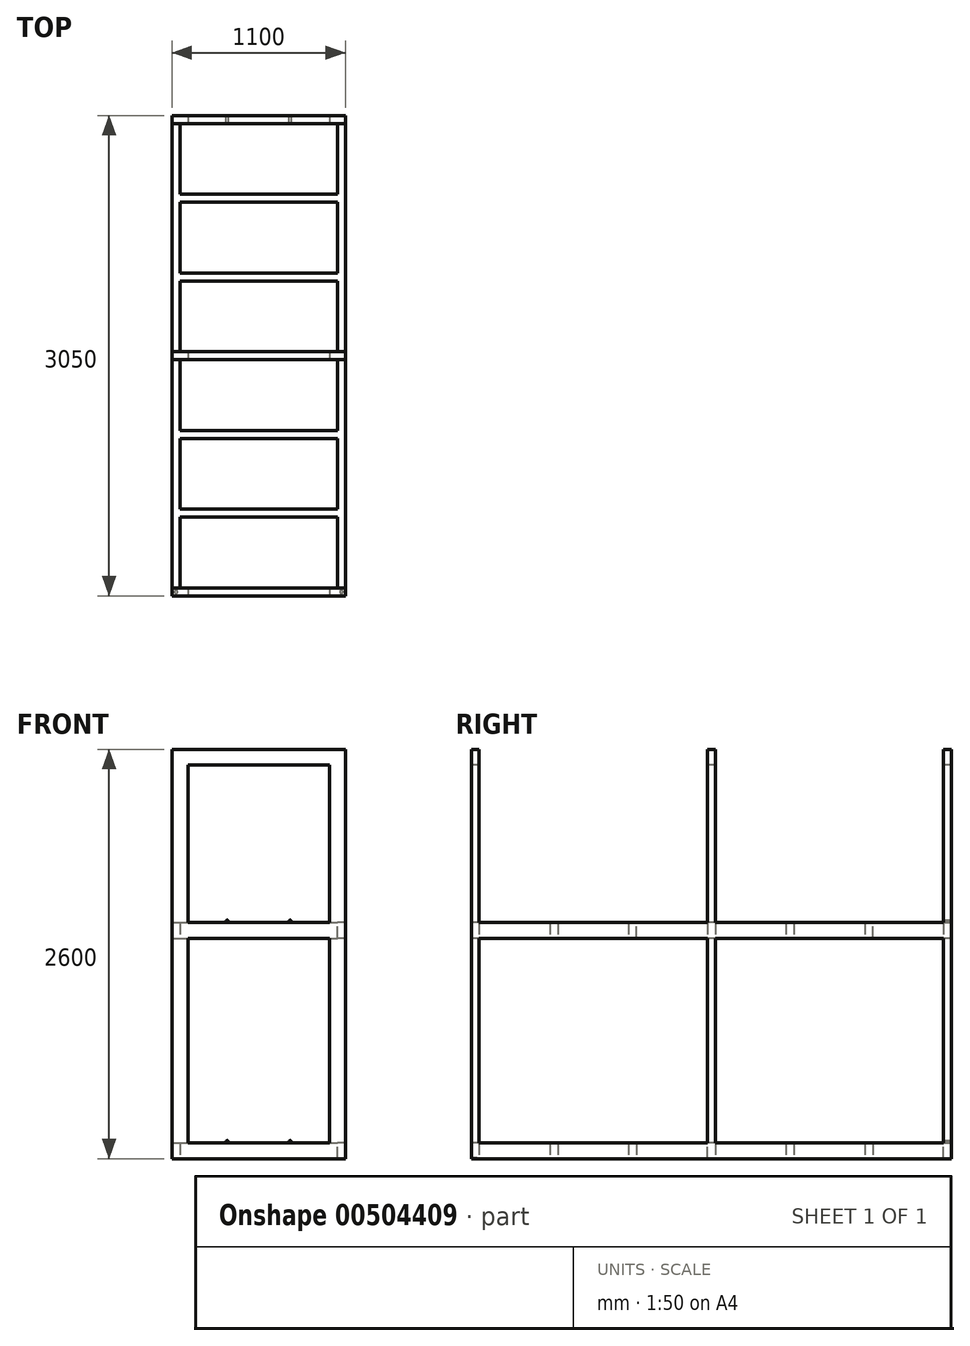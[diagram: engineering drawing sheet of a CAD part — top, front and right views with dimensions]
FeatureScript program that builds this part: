
annotation { "Feature Type Name" : "Feature", "Feature Type Description" : "" }
export const myFeature = defineFeature(function(context is Context, id is Id, definition is map)
    precondition{}
    {
        {
            var Q0;
            Q0=qCreatedBy(makeId("Front.planeOp"),FACE);
            var sketch = newSketch(context, id + "F0", { "sketchPlane" : qUnion([Q0])});
            skCircle(sketch, "E0", {"center": v(0, 700) * mm, "radius": 600 * mm});
            skCircle(sketch, "E1", {"center": v(0, 2100) * mm, "radius": 600 * mm});
            skSolve(sketch);
        }
        {
            var Q0;
            Q0=qCreatedBy(makeId("Front.planeOp"),FACE);
            var sketch = newSketch(context, id + "F1", { "sketchPlane" : qUnion([Q0])});
            skLineSegment(sketch, "E2.bottom", {"start": v(-550, 2600) * mm, "end": v(550, 2600) * mm});
            skLineSegment(sketch, "E2.top", {"start": v(-550, 0) * mm, "end": v(550, 0) * mm});
            skLineSegment(sketch, "E2.left", {"start": v(-550, 2600) * mm, "end": v(-550, 0) * mm});
            skLineSegment(sketch, "E2.right", {"start": v(550, 2600) * mm, "end": v(550, 0) * mm});
            skSolve(sketch);
        }
        {
            var Q0;
            Q0=makeQuery(id+"F1.imprint","IMPRINT",FACE,{"disambiguationData":[TD([[makeQuery(id+"F1.imprint","IMPRINT",EDGE,{"derivedFrom":sQuery(id+"F1.wireOp",EDGE,"E2.bottom")}),-1.0]])]});
            extrude(context, id + "F2", {"entities" : qUnion([Q0]), "depth" : 4550 * mm, "offsetDistance" : 25 * mm});
        }
        {
            var Q0;
            Q0=makeQuery(id+"F2.opExtrude","CAP_FACE",FACE,{"disambiguationData":[OSD([sQuery(id+"F1.wireOp",EDGE,"E2.bottom"),sQuery(id+"F1.wireOp",EDGE,"E2.top"),sQuery(id+"F1.wireOp",EDGE,"E2.left"),sQuery(id+"F1.wireOp",EDGE,"E2.right")])],"isStart":false});
            var sketch = newSketch(context, id + "F3", { "sketchPlane" : qUnion([Q0])});
            skLineSegment(sketch, "E3.bottom", {"start": v(-450, 1400) * mm, "end": v(450, 1400) * mm});
            skLineSegment(sketch, "E3.top", {"start": v(-450, 100) * mm, "end": v(450, 100) * mm});
            skLineSegment(sketch, "E3.left", {"start": v(-450, 1400) * mm, "end": v(-450, 100) * mm});
            skLineSegment(sketch, "E3.right", {"start": v(450, 1400) * mm, "end": v(450, 100) * mm});
            skLineSegment(sketch, "E4.top", {"start": v(-450, 1500) * mm, "end": v(450, 1500) * mm});
            skLineSegment(sketch, "E5.bottom", {"start": v(-450, 2500) * mm, "end": v(450, 2500) * mm});
            skLineSegment(sketch, "E6", {"start": v(-450, 1500) * mm, "end": v(-450, 2500) * mm});
            skLineSegment(sketch, "E7", {"start": v(450, 2500) * mm, "end": v(450, 1500) * mm});
            skSolve(sketch);
        }
        {
            var Q0;
            Q0=qSketchRegion(id+"F3",true);
            extrude(context, id + "F4", {"entities" : qUnion([Q0]), "operationType" : NewBodyOperationType.REMOVE, "oppositeDirection" : true, "depth" : 20000 * mm, "offsetDistance" : 25 * mm});
        }
        {
            var Q0;
            Q0=makeQuery(id+"F2.opExtrude","SWEPT_FACE",FACE,{"disambiguationData":[OSD([sQuery(id+"F1.wireOp",EDGE,"E2.right")])]});
            var sketch = newSketch(context, id + "F5", { "sketchPlane" : qUnion([Q0])});
            skLineSegment(sketch, "E8.bottom", {"start": v(-1550, 4014.4) * mm, "end": v(-3000, 4014.4) * mm});
            skLineSegment(sketch, "E8.top", {"start": v(-1550, -275.7) * mm, "end": v(-3000, -275.7) * mm});
            skLineSegment(sketch, "E8.left", {"start": v(-1550, 4014.4) * mm, "end": v(-1550, -275.7) * mm});
            skLineSegment(sketch, "E8.right", {"start": v(-3000, 4014.4) * mm, "end": v(-3000, -275.7) * mm});
            skLineSegment(sketch, "E9.bottom", {"start": v(-3050, 4012.1) * mm, "end": v(-4500, 4012.1) * mm});
            skLineSegment(sketch, "E9.top", {"start": v(-3050, -275.7) * mm, "end": v(-4500, -275.7) * mm});
            skLineSegment(sketch, "E9.left", {"start": v(-3050, 4012.1) * mm, "end": v(-3050, -275.7) * mm});
            skLineSegment(sketch, "E9.right", {"start": v(-4500, 4012.1) * mm, "end": v(-4500, -275.7) * mm});
            skSolve(sketch);
        }
        {
            var Q0;
            Q0=qSketchRegion(id+"F5",true);
            extrude(context, id + "F6", {"entities" : qUnion([Q0]), "operationType" : NewBodyOperationType.REMOVE, "oppositeDirection" : true, "depth" : 2000 * mm, "offsetDistance" : 25 * mm});
        }
        {
            var Q0;
            Q0=makeQuery(id+"F2.opExtrude","CAP_FACE",FACE,{"disambiguationData":[OSD([sQuery(id+"F1.wireOp",EDGE,"E2.bottom"),sQuery(id+"F1.wireOp",EDGE,"E2.top"),sQuery(id+"F1.wireOp",EDGE,"E2.left"),sQuery(id+"F1.wireOp",EDGE,"E2.right")])],"isStart":false});
            var sketch = newSketch(context, id + "F7", { "sketchPlane" : qUnion([Q0])});
            skLineSegment(sketch, "E10.bottom", {"start": v(550, 1500) * mm, "end": v(500, 1500) * mm});
            skLineSegment(sketch, "E10.top", {"start": v(550, 1400) * mm, "end": v(500, 1400) * mm});
            skLineSegment(sketch, "E10.left", {"start": v(550, 1500) * mm, "end": v(550, 1400) * mm});
            skLineSegment(sketch, "E10.right", {"start": v(500, 1500) * mm, "end": v(500, 1400) * mm});
            skLineSegment(sketch, "E11.left", {"start": v(550, 1500) * mm, "end": v(550, 1500) * mm});
            skLineSegment(sketch, "E11.right", {"start": v(500, 1500) * mm, "end": v(500, 1500) * mm});
            skLineSegment(sketch, "E12.bottom", {"start": v(-550, 1500) * mm, "end": v(-500, 1500) * mm});
            skLineSegment(sketch, "E12.top", {"start": v(-550, 1400) * mm, "end": v(-500, 1400) * mm});
            skLineSegment(sketch, "E12.left", {"start": v(-550, 1500) * mm, "end": v(-550, 1400) * mm});
            skLineSegment(sketch, "E12.right", {"start": v(-500, 1500) * mm, "end": v(-500, 1400) * mm});
            skLineSegment(sketch, "E13.bottom", {"start": v(-550, 0) * mm, "end": v(-500, 0) * mm});
            skLineSegment(sketch, "E13.top", {"start": v(-550, 100) * mm, "end": v(-500, 100) * mm});
            skLineSegment(sketch, "E13.left", {"start": v(-550, 0) * mm, "end": v(-550, 100) * mm});
            skLineSegment(sketch, "E13.right", {"start": v(-500, 0) * mm, "end": v(-500, 100) * mm});
            skLineSegment(sketch, "E14.bottom", {"start": v(550, 100) * mm, "end": v(500, 100) * mm});
            skLineSegment(sketch, "E14.top", {"start": v(550, 0) * mm, "end": v(500, 0) * mm});
            skLineSegment(sketch, "E14.left", {"start": v(550, 100) * mm, "end": v(550, 0) * mm});
            skLineSegment(sketch, "E14.right", {"start": v(500, 100) * mm, "end": v(500, 0) * mm});
            skSolve(sketch);
        }
        {
            var Q0;
            Q0=qSketchRegion(id+"F7",true);
            extrude(context, id + "F8", {"entities" : qUnion([Q0]), "operationType" : NewBodyOperationType.ADD, "oppositeDirection" : true, "depth" : 4550 * mm, "offsetDistance" : 25 * mm});
        }
        {
            var Q0;
            Q0=makeQuery(id+"F2.opExtrude","CAP_FACE",FACE,{"disambiguationData":[OSD([sQuery(id+"F1.wireOp",EDGE,"E2.bottom"),sQuery(id+"F1.wireOp",EDGE,"E2.top"),sQuery(id+"F1.wireOp",EDGE,"E2.left"),sQuery(id+"F1.wireOp",EDGE,"E2.right")])],"isStart":true});
            var sketch = newSketch(context, id + "F9", { "sketchPlane" : qUnion([Q0])});
            skCircle(sketch, "E15", {"center": v(200, 1507.5) * mm, "radius": 7.5 * mm});
            skCircle(sketch, "E16", {"center": v(-200, 1507.5) * mm, "radius": 7.5 * mm});
            skCircle(sketch, "E17", {"center": v(200, 107.5) * mm, "radius": 7.5 * mm});
            skCircle(sketch, "E18", {"center": v(-200, 107.5) * mm, "radius": 7.5 * mm});
            skSolve(sketch);
        }
        {
            var Q0;
            {var subQ1=sQuery(id+"F1.wireOp",EDGE,"E2.right");Q0=makeQuery(id+"F8.boolean.opBoolean","MERGE",FACE,{"derivedFrom":[makeQuery(id+"F6.boolean.opBoolean","SPLIT",FACE,{"disambiguationData":[TD([makeQuery(id+"F6.opExtrude","SWEPT_FACE",FACE,{"disambiguationData":[OSD([sQuery(id+"F5.wireOp",EDGE,"E9.right")])]})])],"derivedFrom":makeQuery(id+"F2.opExtrude","SWEPT_FACE",FACE,{"disambiguationData":[OSD([subQ1])]})}),makeQuery(id+"F8.opExtrude","SWEPT_FACE",FACE,{"disambiguationData":[OSD([sQuery(id+"F7.wireOp",EDGE,"E10.left")])]}),makeQuery(id+"F8.opExtrude","SWEPT_FACE",FACE,{"disambiguationData":[OSD([sQuery(id+"F7.wireOp",EDGE,"E14.left")])]}),makeQuery(id+"F8.opExtrude","SWEPT_FACE",FACE,{"disambiguationData":[OSD([sQuery(id+"F7.wireOp",EDGE,"wLybgxwT-SlUP-khaT-fIYV-JsbXyBy0HU9R.right")])]})]});}
            var sketch = newSketch(context, id + "F10", { "sketchPlane" : qUnion([Q0])});
            skLineSegment(sketch, "E19.top", {"start": v(-2550, 1500) * mm, "end": v(-2500, 1500) * mm});
            skLineSegment(sketch, "E20.bottom", {"start": v(-2050, 1400) * mm, "end": v(-2000, 1400) * mm});
            skLineSegment(sketch, "E21.bottom", {"start": v(-4050, 1500) * mm, "end": v(-4000, 1500) * mm});
            skLineSegment(sketch, "E21.top", {"start": v(-4050, 1400) * mm, "end": v(-4000, 1400) * mm});
            skLineSegment(sketch, "E21.left", {"start": v(-4050, 1500) * mm, "end": v(-4050, 1400) * mm});
            skLineSegment(sketch, "E21.right", {"start": v(-4000, 1500) * mm, "end": v(-4000, 1400) * mm});
            skLineSegment(sketch, "E22.bottom", {"start": v(-3550, 1500) * mm, "end": v(-3500, 1500) * mm});
            skLineSegment(sketch, "E22.top", {"start": v(-3550, 1400) * mm, "end": v(-3500, 1400) * mm});
            skLineSegment(sketch, "E22.left", {"start": v(-3550, 1500) * mm, "end": v(-3550, 1400) * mm});
            skLineSegment(sketch, "E22.right", {"start": v(-3500, 1500) * mm, "end": v(-3500, 1400) * mm});
            skLineSegment(sketch, "E23.top", {"start": v(-2550, 1400) * mm, "end": v(-2500, 1400) * mm});
            skLineSegment(sketch, "E23.left", {"start": v(-2550, 1500) * mm, "end": v(-2550, 1400) * mm});
            skLineSegment(sketch, "E23.right", {"start": v(-2500, 1500) * mm, "end": v(-2500, 1400) * mm});
            skLineSegment(sketch, "E24.bottom", {"start": v(-2050, 1500) * mm, "end": v(-2000, 1500) * mm});
            skLineSegment(sketch, "E24.left", {"start": v(-2050, 1500) * mm, "end": v(-2050, 1400) * mm});
            skLineSegment(sketch, "E24.right", {"start": v(-2000, 1500) * mm, "end": v(-2000, 1400) * mm});
            skLineSegment(sketch, "E25.bottom", {"start": v(-4050, 100) * mm, "end": v(-4000, 100) * mm});
            skLineSegment(sketch, "E25.top", {"start": v(-4050, 0) * mm, "end": v(-4000, 0) * mm});
            skLineSegment(sketch, "E25.left", {"start": v(-4050, 100) * mm, "end": v(-4050, 0) * mm});
            skLineSegment(sketch, "E25.right", {"start": v(-4000, 100) * mm, "end": v(-4000, 0) * mm});
            skLineSegment(sketch, "E26.bottom", {"start": v(-3550, 100) * mm, "end": v(-3500, 100) * mm});
            skLineSegment(sketch, "E26.top", {"start": v(-3550, 0) * mm, "end": v(-3500, 0) * mm});
            skLineSegment(sketch, "E26.left", {"start": v(-3550, 100) * mm, "end": v(-3550, 0) * mm});
            skLineSegment(sketch, "E26.right", {"start": v(-3500, 100) * mm, "end": v(-3500, 0) * mm});
            skLineSegment(sketch, "E27.bottom", {"start": v(-2550, 100) * mm, "end": v(-2499.8, 100) * mm});
            skLineSegment(sketch, "E27.top", {"start": v(-2550, 0) * mm, "end": v(-2499.8, 0) * mm});
            skLineSegment(sketch, "E27.left", {"start": v(-2550, 100) * mm, "end": v(-2550, 0) * mm});
            skLineSegment(sketch, "E27.right", {"start": v(-2499.8, 100) * mm, "end": v(-2499.8, 0) * mm});
            skLineSegment(sketch, "E28.bottom", {"start": v(-2049.8, 100) * mm, "end": v(-2000, 100) * mm});
            skLineSegment(sketch, "E28.top", {"start": v(-2049.8, 0) * mm, "end": v(-2000, 0) * mm});
            skLineSegment(sketch, "E28.left", {"start": v(-2049.8, 100) * mm, "end": v(-2049.8, 0) * mm});
            skLineSegment(sketch, "E28.right", {"start": v(-2000, 100) * mm, "end": v(-2000, 0) * mm});
            skSolve(sketch);
        }
        {
            var Q0;
            Q0=qSketchRegion(id+"F10",true);
            var Q1;
            Q1=makeQuery(id+"F8.boolean.opBoolean","SPLIT",FACE,{"disambiguationData":[TD([makeQuery(id+"F6.boolean.opBoolean","COPY",FACE,{"derivedFrom":makeQuery(id+"F6.opExtrude","SWEPT_FACE",FACE,{"disambiguationData":[OSD([sQuery(id+"F5.wireOp",EDGE,"E9.left")])]})})])],"derivedFrom":makeQuery(id+"F8.opExtrude","SWEPT_FACE",FACE,{"disambiguationData":[OSD([sQuery(id+"F7.wireOp",EDGE,"E12.right")])]})});
            extrude(context, id + "F11", {"entities" : qUnion([Q0]), "operationType" : NewBodyOperationType.ADD, "endBound" : BoundingType.UP_TO_SURFACE, "oppositeDirection" : true, "depth" : 1500 * mm, "endBoundEntityFace" : qUnion([Q1]), "offsetDistance" : 25 * mm});
        }
        {
            var Q0;
            Q0=qSketchRegion(id+"F9",true);
            var Q1;
            Q1=makeQuery(id+"F6.boolean.opBoolean","COPY",FACE,{"derivedFrom":makeQuery(id+"F6.opExtrude","SWEPT_FACE",FACE,{"disambiguationData":[OSD([sQuery(id+"F5.wireOp",EDGE,"E8.left")])]})});
            extrude(context, id + "F12", {"entities" : qUnion([Q0]), "operationType" : NewBodyOperationType.ADD, "endBound" : BoundingType.UP_TO_SURFACE, "oppositeDirection" : true, "depth" : 50 * mm, "endBoundEntityFace" : qUnion([Q1]), "offsetDistance" : 25 * mm});
        }
        {
            var Q0;
            {var subQ4=sQuery(id+"F1.wireOp",EDGE,"E2.right");var subQ5=makeQuery(id+"F2.opExtrude","SWEPT_FACE",FACE,{"disambiguationData":[OSD([subQ4])]});Q0=makeQuery(id+"F8.boolean.opBoolean","MERGE",FACE,{"derivedFrom":[makeQuery(id+"F6.boolean.opBoolean","SPLIT",FACE,{"disambiguationData":[TD([makeQuery(id+"F6.opExtrude","SWEPT_FACE",FACE,{"disambiguationData":[OSD([sQuery(id+"F5.wireOp",EDGE,"E8.left")])]})])],"derivedFrom":subQ5}),makeQuery(id+"F6.boolean.opBoolean","SPLIT",FACE,{"disambiguationData":[TD([makeQuery(id+"F6.opExtrude","SWEPT_FACE",FACE,{"disambiguationData":[OSD([sQuery(id+"F5.wireOp",EDGE,"E9.right")])]})])],"derivedFrom":subQ5}),makeQuery(id+"F6.boolean.opBoolean","SPLIT",FACE,{"disambiguationData":[TD([makeQuery(id+"F6.opExtrude","SWEPT_FACE",FACE,{"disambiguationData":[OSD([sQuery(id+"F5.wireOp",EDGE,"E8.right")])]})])],"derivedFrom":subQ5}),makeQuery(id+"F8.opExtrude","SWEPT_FACE",FACE,{"disambiguationData":[OSD([sQuery(id+"F7.wireOp",EDGE,"E10.left")])]}),makeQuery(id+"F8.opExtrude","SWEPT_FACE",FACE,{"disambiguationData":[OSD([sQuery(id+"F7.wireOp",EDGE,"E14.left")])]})]});}
            var sketch = newSketch(context, id + "F13", { "sketchPlane" : qUnion([Q0])});
            skLineSegment(sketch, "E29.bottom", {"start": v(120.94, 2600) * mm, "end": v(-1500, 2600) * mm});
            skLineSegment(sketch, "E29.top", {"start": v(120.94, 0) * mm, "end": v(-1500, 0) * mm});
            skLineSegment(sketch, "E29.left", {"start": v(120.94, 2600) * mm, "end": v(120.94, 0) * mm});
            skLineSegment(sketch, "E29.right", {"start": v(-1500, 2600) * mm, "end": v(-1500, 0) * mm});
            skSolve(sketch);
        }
        {
            var Q0;
            Q0 = qSketchRegion(id + "F13", true);
            extrude(context, id + "F14", {"entities" : qUnion([Q0]), "operationType" : NewBodyOperationType.REMOVE, "oppositeDirection" : true, "depth" : 1200 * mm, "offsetDistance" : 25 * mm});
        }
        {
            var Q0;
            {var subQ4=sQuery(id+"F1.wireOp",EDGE,"E2.top");var subQ5=makeQuery(id+"F2.opExtrude","SWEPT_FACE",FACE,{"disambiguationData":[OSD([subQ4])]});Q0=makeQuery(id+"F11.boolean.opBoolean","MERGE",FACE,{"derivedFrom":[makeQuery(id+"F8.boolean.opBoolean","MERGE",FACE,{"derivedFrom":[makeQuery(id+"F6.boolean.opBoolean","SPLIT",FACE,{"disambiguationData":[TD([makeQuery(id+"F6.opExtrude","SWEPT_FACE",FACE,{"disambiguationData":[OSD([sQuery(id+"F5.wireOp",EDGE,"E8.left")])]})])],"derivedFrom":subQ5}),makeQuery(id+"F6.boolean.opBoolean","SPLIT",FACE,{"disambiguationData":[TD([makeQuery(id+"F6.opExtrude","SWEPT_FACE",FACE,{"disambiguationData":[OSD([sQuery(id+"F5.wireOp",EDGE,"E9.right")])]})])],"derivedFrom":subQ5}),makeQuery(id+"F6.boolean.opBoolean","SPLIT",FACE,{"disambiguationData":[TD([makeQuery(id+"F6.opExtrude","SWEPT_FACE",FACE,{"disambiguationData":[OSD([sQuery(id+"F5.wireOp",EDGE,"E8.right")])]})])],"derivedFrom":subQ5}),makeQuery(id+"F8.opExtrude","SWEPT_FACE",FACE,{"disambiguationData":[OSD([sQuery(id+"F7.wireOp",EDGE,"E13.bottom")])]}),makeQuery(id+"F8.opExtrude","SWEPT_FACE",FACE,{"disambiguationData":[OSD([sQuery(id+"F7.wireOp",EDGE,"E14.top")])]})]}),makeQuery(id+"F11.opExtrude","SWEPT_FACE",FACE,{"disambiguationData":[OSD([sQuery(id+"F10.wireOp",EDGE,"E25.top")])]}),makeQuery(id+"F11.opExtrude","SWEPT_FACE",FACE,{"disambiguationData":[OSD([sQuery(id+"F10.wireOp",EDGE,"E26.top")])]}),makeQuery(id+"F11.opExtrude","SWEPT_FACE",FACE,{"disambiguationData":[OSD([sQuery(id+"F10.wireOp",EDGE,"E27.top")])]}),makeQuery(id+"F11.opExtrude","SWEPT_FACE",FACE,{"disambiguationData":[OSD([sQuery(id+"F10.wireOp",EDGE,"E28.top")])]})]});}
            var sketch = newSketch(context, id + "F15", { "sketchPlane" : qUnion([Q0])});
            skCircle(sketch, "E30", {"center": v(525, 4525) * mm, "radius": 10 * mm});
            skCircle(sketch, "E31", {"center": v(-525, 4525) * mm, "radius": 10 * mm});
            skSolve(sketch);
        }
        {
            var Q0;
            Q0 = qSketchRegion(id + "F15", true);
            extrude(context, id + "F16", {"entities" : qUnion([Q0]), "operationType" : NewBodyOperationType.REMOVE, "oppositeDirection" : true, "depth" : 5 * mm, "offsetDistance" : 25 * mm});
        }
    });
